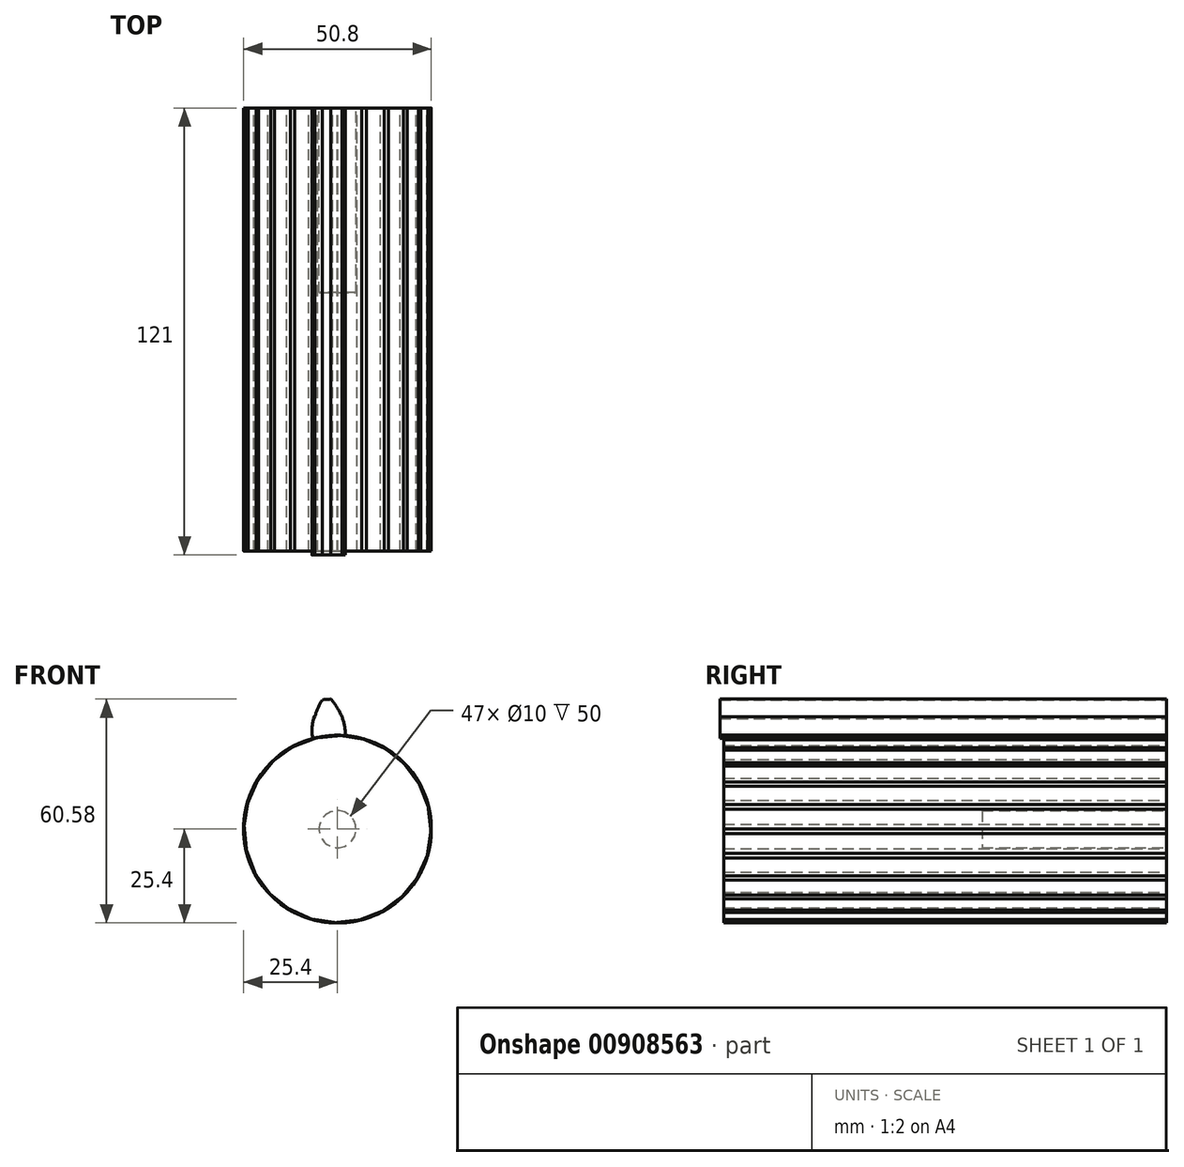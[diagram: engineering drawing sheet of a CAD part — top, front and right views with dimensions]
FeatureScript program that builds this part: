
annotation { "Feature Type Name" : "Feature", "Feature Type Description" : "" }
export const myFeature = defineFeature(function(context is Context, id is Id, definition is map)
    precondition{}
    {
        {
            var Q0;
            Q0=qCreatedBy(makeId("Front.planeOp"),FACE);
            var sketch = newSketch(context, id + "F0", { "sketchPlane" : qUnion([Q0])});
            skCircle(sketch, "E0", {"center": v(0, 0) * mm, "radius": 29.21 * mm, "construction": true});
            skCircle(sketch, "E1", {"center": v(0, 0) * mm, "radius": 27.94 * mm, "construction": true});
            skCircle(sketch, "E2", {"center": v(0, 0) * mm, "radius": 25.4 * mm});
            skLineSegment(sketch, "E3", {"start": v(0, 0) * mm, "end": v(0, 113.9) * mm, "construction": true});
            skLineSegment(sketch, "E4", {"start": v(0, 0) * mm, "end": v(-7.6, 116.01) * mm, "construction": true});
            skLineSegment(sketch, "E5", {"start": v(0, 27.94) * mm, "end": v(-127.04, 27.94) * mm, "construction": true});
            skLineSegment(sketch, "E6", {"start": v(0, 27.94) * mm, "end": v(-129.75, -19.29) * mm, "construction": true});
            skCircle(sketch, "E7", {"center": v(0, 0) * mm, "radius": 26.26 * mm, "construction": true});
            skCircle(sketch, "E8", {"center": v(0, 27.94) * mm, "radius": 14.6 * mm, "construction": true});
            skCircle(sketch, "E9", {"center": v(-13.55, 22.49) * mm, "radius": 14.6 * mm, "construction": true});
            skArc(sketch, "E10", {"start": v(1.2, 30.43) * mm, "mid": v(-0.08, 32.94) * mm, "end": v(-1.79, 35.18) * mm});
            skArc(sketch, "E11", {"start": v(2.18, 25.47) * mm, "mid": v(1.9, 27.99) * mm, "end": v(1.2, 30.43) * mm});
            skArc(sketch, "E12", {"start": v(1.2, 30.43) * mm, "mid": v(-0.1, 32.92) * mm, "end": v(-1.79, 35.18) * mm});
            skArc(sketch, "E13.MirrorCS", {"start": v(-6.11, 30.47) * mm, "mid": v(-5.27, 32.82) * mm, "end": v(-4.11, 35.03) * mm});
            skArc(sketch, "E14.MirrorCS", {"start": v(-6.77, 24.88) * mm, "mid": v(-6.88, 27.42) * mm, "end": v(-6.46, 29.93) * mm});
            skArc(sketch, "E15", {"start": v(-4.11, 35.03) * mm, "mid": v(-2.95, 35.08) * mm, "end": v(-1.79, 35.18) * mm});
            skLineSegment(sketch, "E16", {"start": v(-6.11, 30.47) * mm, "end": v(-6.46, 29.93) * mm});
            skLineSegment(sketch, "E17", {"start": v(-6.77, 24.88) * mm, "end": v(-6.64, 24.52) * mm});
            skLineSegment(sketch, "E18", {"start": v(-6.64, 24.52) * mm, "end": v(2.18, 25.47) * mm});
            skSolve(sketch);
        }
        {
            var Q0;
            {var subQ0=sQuery(id+"F0.wireOp",EDGE,"E2");var subQ2=makeQuery(id+"F0.imprint","INTERSECT",VERTEX,{"derivedFrom":[subQ0,sQuery(id+"F0.wireOp",EDGE,"b6d96da9-ef11-4cbd-a089-e09cc05b45860.MirrorCS")]});Q0=makeQuery(id+"F0.imprint","IMPRINT",FACE,{"disambiguationData":[TD([[makeQuery(id+"F0.imprint","IMPRINT",EDGE,{"disambiguationData":[TD([[subQ2,1.0]])],"derivedFrom":subQ0}),1.0]])]});}
            var Q1;
            {var subQ0=sQuery(id+"F0.wireOp",EDGE,"uWEVJ2n1-65r1-nzhM-PK69-QDBhP6fbYYYu");Q1=makeQuery(id+"F0.imprint","IMPRINT",FACE,{"disambiguationData":[TD([[makeQuery(id+"F0.imprint","IMPRINT",EDGE,{"derivedFrom":subQ0}),1.0]])]});}
            extrude(context, id + "F1", {"entities" : qUnion([Q0, Q1]), "depth" : 120 * mm, "offsetDistance" : 25.4 * mm});
        }
        {
            var Q0;
            Q0=makeQuery(id+"F1.opExtrude","SWEPT_BODY",BODY,{"disambiguationData":[OSD([sQuery(id+"F0.wireOp",EDGE,"E2"),sQuery(id+"F0.wireOp",EDGE,"uWEVJ2n1-65r1-nzhM-PK69-QDBhP6fbYYYu"),sQuery(id+"F0.wireOp",EDGE,"TzWsQwoT-ipm3-9mWc-yn9i-VSCpHPm2UVmG"),sQuery(id+"F0.wireOp",EDGE,"6f94443d-2c7b-4fe5-9b55-edac45d44a1e0.MirrorCS"),sQuery(id+"F0.wireOp",EDGE,"b6d96da9-ef11-4cbd-a089-e09cc05b45860.MirrorCS"),sQuery(id+"F0.wireOp",EDGE,"eqr2v48K-f3aY-UyOG-eX6m-u15Z69JRCI6n")])]});
            var Q1;
            Q1=makeQuery(id+"F1.opExtrude","SWEPT_FACE",FACE,{"disambiguationData":[OSD([sQuery(id+"F0.wireOp",EDGE,"E2")])]});
            circularPattern(context, id + "F2", {"entities" : qUnion([Q0]), "axis" : qUnion([Q1]), "angle" : 15 * degree, "instanceCount" : 24, "isCentered" : true});
        }
        {
            var Q0;
            Q0=makeQuery(id+"F1.opExtrude","CAP_FACE",FACE,{"disambiguationData":[OSD([sQuery(id+"F0.wireOp",EDGE,"E2"),sQuery(id+"F0.wireOp",EDGE,"uWEVJ2n1-65r1-nzhM-PK69-QDBhP6fbYYYu"),sQuery(id+"F0.wireOp",EDGE,"TzWsQwoT-ipm3-9mWc-yn9i-VSCpHPm2UVmG"),sQuery(id+"F0.wireOp",EDGE,"6f94443d-2c7b-4fe5-9b55-edac45d44a1e0.MirrorCS"),sQuery(id+"F0.wireOp",EDGE,"b6d96da9-ef11-4cbd-a089-e09cc05b45860.MirrorCS"),sQuery(id+"F0.wireOp",EDGE,"eqr2v48K-f3aY-UyOG-eX6m-u15Z69JRCI6n")])],"isStart":true});
            var sketch = newSketch(context, id + "F3", { "sketchPlane" : qUnion([Q0])});
            skCircle(sketch, "E19", {"center": v(0, 0) * mm, "radius": 5 * mm});
            skSolve(sketch);
        }
        {
            var Q0;
            Q0=makeQuery(id+"F3.imprint","IMPRINT",FACE,{"disambiguationData":[TD([[makeQuery(id+"F3.imprint","IMPRINT",EDGE,{"derivedFrom":sQuery(id+"F3.wireOp",EDGE,"E19")}),1.0]])]});
            extrude(context, id + "F4", {"entities" : qUnion([Q0]), "operationType" : NewBodyOperationType.REMOVE, "oppositeDirection" : true, "depth" : 50 * mm, "offsetDistance" : 25 * mm});
        }
        {
            var Q0;
            {var subQ0=sQuery(id+"F0.wireOp",EDGE,"E11");Q0=makeQuery(id+"F0.imprint","IMPRINT",FACE,{"disambiguationData":[TD([[makeQuery(id+"F0.imprint","IMPRINT",EDGE,{"derivedFrom":subQ0}),1.0]])]});}
            extrude(context, id + "F5", {"entities" : qUnion([Q0]), "depth" : 121 * mm, "offsetDistance" : 25 * mm});
        }
    });
